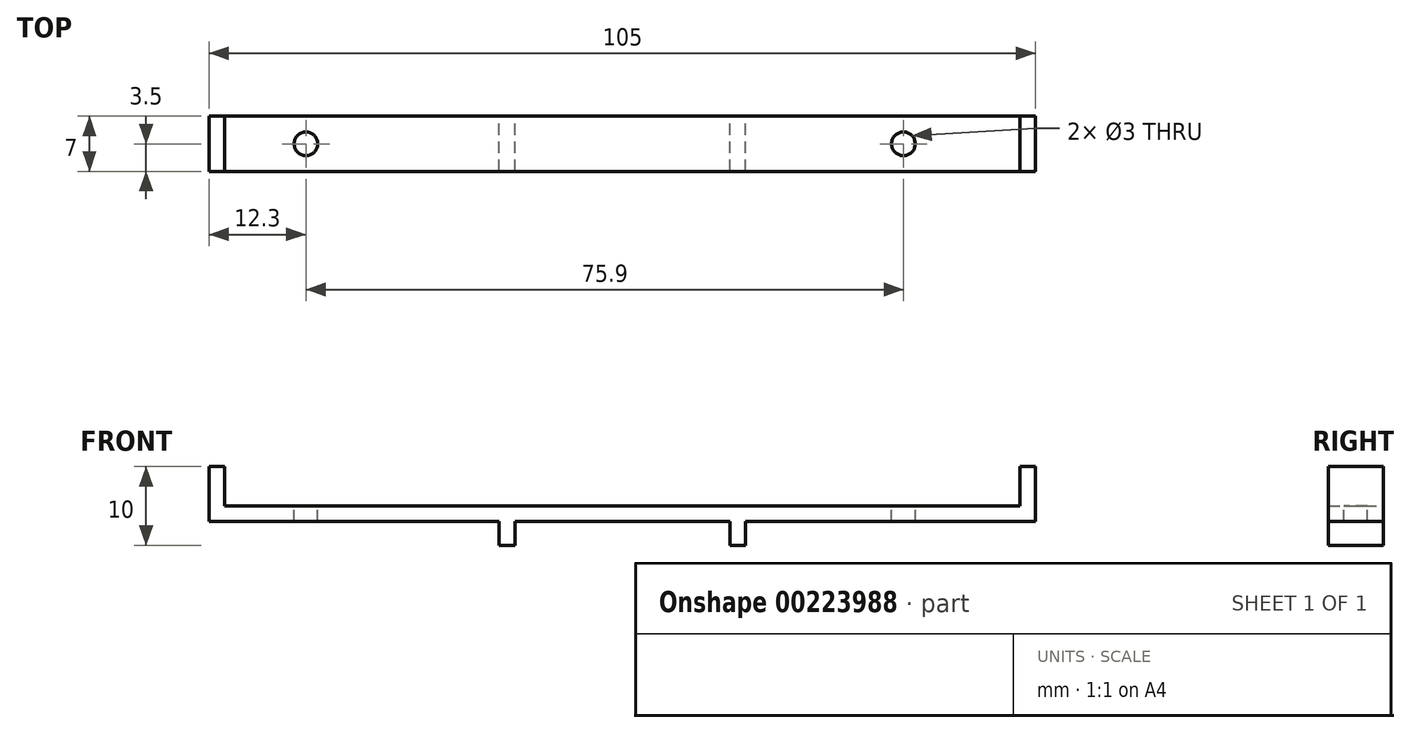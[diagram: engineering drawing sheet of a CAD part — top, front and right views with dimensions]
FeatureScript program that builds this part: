
annotation { "Feature Type Name" : "Feature", "Feature Type Description" : "" }
export const myFeature = defineFeature(function(context is Context, id is Id, definition is map)
    precondition{}
    {
        {
            var Q0;
            Q0=qCreatedBy(makeId("Front.planeOp"),FACE);
            var sketch = newSketch(context, id + "F0", { "sketchPlane" : qUnion([Q0])});
            skLineSegment(sketch, "E0.bottom", {"start": v(50.5, 3.5) * mm, "end": v(-50.5, 3.5) * mm});
            skLineSegment(sketch, "E0.top", {"start": v(50.5, 1.5) * mm, "end": v(15.65, 1.5) * mm});
            skLineSegment(sketch, "E1", {"start": v(-13.65, 1.5) * mm, "end": v(-13.65, -1.5) * mm});
            skLineSegment(sketch, "E2", {"start": v(13.65, 1.5) * mm, "end": v(13.65, -1.5) * mm});
            skLineSegment(sketch, "E3", {"start": v(13.65, -1.5) * mm, "end": v(15.65, -1.5) * mm});
            skLineSegment(sketch, "E4", {"start": v(15.65, -1.5) * mm, "end": v(15.65, 1.5) * mm});
            skLineSegment(sketch, "E5", {"start": v(-13.65, -1.5) * mm, "end": v(-15.65, -1.5) * mm});
            skLineSegment(sketch, "E6", {"start": v(-15.65, -1.5) * mm, "end": v(-15.65, 1.5) * mm});
            skLineSegment(sketch, "E7.bottom", {"start": v(-50.5, 1.5) * mm, "end": v(-52.5, 1.5) * mm});
            skLineSegment(sketch, "E7.top", {"start": v(-50.5, 8.5) * mm, "end": v(-52.5, 8.5) * mm});
            skLineSegment(sketch, "E7.left", {"start": v(-50.5, 3.5) * mm, "end": v(-50.5, 8.5) * mm});
            skLineSegment(sketch, "E7.right", {"start": v(-52.5, 1.5) * mm, "end": v(-52.5, 8.5) * mm});
            skLineSegment(sketch, "E8.bottom", {"start": v(50.5, 1.5) * mm, "end": v(52.5, 1.5) * mm});
            skLineSegment(sketch, "E8.top", {"start": v(50.5, 8.5) * mm, "end": v(52.5, 8.5) * mm});
            skLineSegment(sketch, "E8.left", {"start": v(50.5, 3.5) * mm, "end": v(50.5, 8.5) * mm});
            skLineSegment(sketch, "E8.right", {"start": v(52.5, 1.5) * mm, "end": v(52.5, 8.5) * mm});
            skLineSegment(sketch, "E9.trimOffspring", {"start": v(13.65, 1.5) * mm, "end": v(-13.65, 1.5) * mm});
            skLineSegment(sketch, "E10.trimOffspring", {"start": v(-15.65, 1.5) * mm, "end": v(-50.5, 1.5) * mm});
            skLineSegment(sketch, "E11", {"start": v(0, 3.5) * mm, "end": v(0, 1.5) * mm, "construction": true});
            skLineSegment(sketch, "E12", {"start": v(-13.65, 0) * mm, "end": v(13.65, 0) * mm, "construction": true});
            skPoint(sketch, "E13", {"position": v(0, 0) * mm});
            skSolve(sketch);
        }
        {
            var Q0;
            Q0 = qSketchRegion(id + "F0", true);
            extrude(context, id + "F1", {"entities" : qUnion([Q0]), "depth" : 7 * mm});
        }
        {
            var Q0;
            Q0=makeQuery(id+"F1.opExtrude","SWEPT_FACE",FACE,{"disambiguationData":[OSD([sQuery(id+"F0.wireOp",EDGE,"E0.bottom")])]});
            var sketch = newSketch(context, id + "F2", { "sketchPlane" : qUnion([Q0])});
            skLineSegment(sketch, "E14", {"start": v(-50.5, -3.5) * mm, "end": v(50.5, -3.5) * mm, "construction": true});
            skCircle(sketch, "E15", {"center": v(-40.2, -3.5) * mm, "radius": 1.5 * mm});
            skCircle(sketch, "E16", {"center": v(35.7, -3.5) * mm, "radius": 1.5 * mm});
            skSolve(sketch);
        }
        {
            var Q0;
            Q0 = qSketchRegion(id + "F2", true);
            extrude(context, id + "F3", {"entities" : qUnion([Q0]), "operationType" : NewBodyOperationType.REMOVE, "endBound" : BoundingType.THROUGH_ALL, "oppositeDirection" : true, "depth" : 25 * mm});
        }
    });
